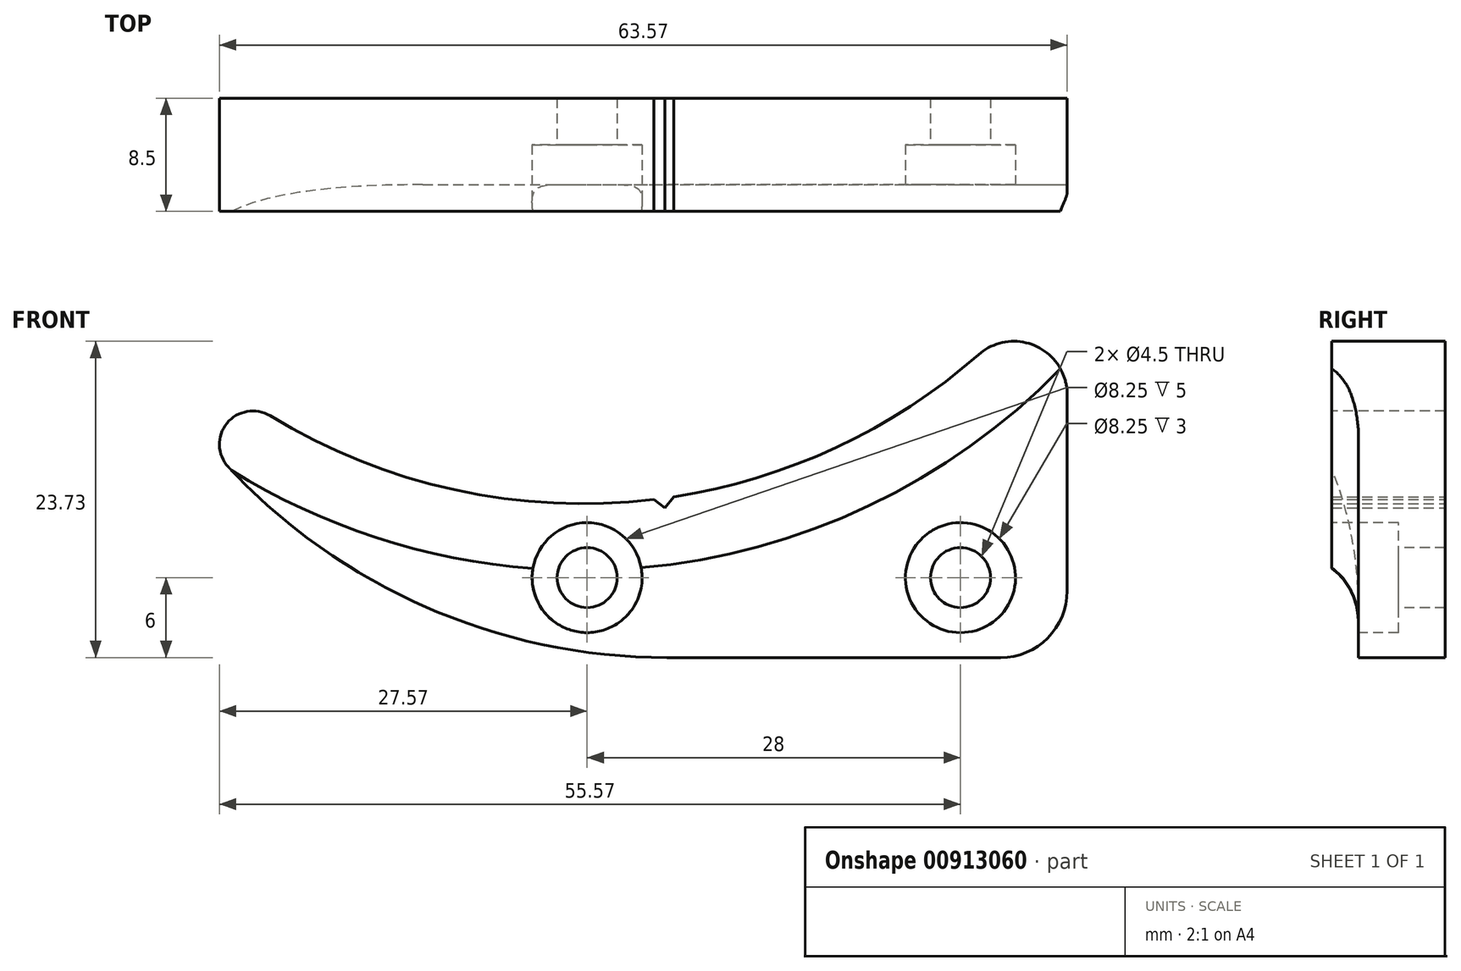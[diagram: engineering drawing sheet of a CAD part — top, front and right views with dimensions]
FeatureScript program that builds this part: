
annotation { "Feature Type Name" : "Feature", "Feature Type Description" : "" }
export const myFeature = defineFeature(function(context is Context, id is Id, definition is map)
    precondition{}
    {
        {
            var Q0;
            Q0=qCreatedBy(makeId("Front.planeOp"),FACE);
            var sketch = newSketch(context, id + "F0", { "sketchPlane" : qUnion([Q0])});
            skLineSegment(sketch, "E0", {"start": v(0, 30) * mm, "end": v(0, 0) * mm});
            skLineSegment(sketch, "E1", {"start": v(0, 0) * mm, "end": v(-30, 0) * mm});
            skArc(sketch, "E2", {"start": v(-72.2, 29.38) * mm, "mid": v(-55.71, 8.07) * mm, "end": v(-30, 0) * mm});
            skArc(sketch, "E3", {"start": v(-72.2, 29.38) * mm, "mid": v(-35.95, 11.55) * mm, "end": v(0, 30) * mm});
            skLineSegment(sketch, "E4", {"start": v(-30, 0) * mm, "end": v(-30, 12) * mm, "construction": true});
            skSolve(sketch);
        }
        {
            var Q0;
            Q0=makeQuery(id+"F0.imprint","IMPRINT",FACE,{"disambiguationData":[TD([[makeQuery(id+"F0.imprint","IMPRINT",EDGE,{"derivedFrom":sQuery(id+"F0.wireOp",EDGE,"E0")}),-1.0]])]});
            extrude(context, id + "F1", {"entities" : qUnion([Q0]), "depth" : 8.5 * mm, "offsetDistance" : 25 * mm});
        }
        {
            var Q0;
            Q0=makeQuery(id+"F1.opExtrude","SWEPT_EDGE",EDGE,{"disambiguationData":[OSD([sQuery(id+"F0.wireOp",EDGE,"E2"),sQuery(id+"F0.wireOp",EDGE,"E3")])]});
            fillet(context, id + "F2", {"entities" : qUnion([Q0]), "radius" : 2.5 * mm, "tangentPropagation" : true, "allowEdgeOverflow" : false});
        }
        {
            var Q0;
            Q0=makeQuery(id+"F1.opExtrude","SWEPT_EDGE",EDGE,{"disambiguationData":[OSD([sQuery(id+"F0.wireOp",EDGE,"E0"),sQuery(id+"F0.wireOp",EDGE,"E3")])]});
            fillet(context, id + "F3", {"entities" : qUnion([Q0]), "radius" : 4 * mm, "tangentPropagation" : true, "allowEdgeOverflow" : false});
        }
        {
            var Q0;
            Q0=makeQuery(id+"F1.opExtrude","CAP_FACE",FACE,{"disambiguationData":[OSD([sQuery(id+"F0.wireOp",EDGE,"E0"),sQuery(id+"F0.wireOp",EDGE,"E1"),sQuery(id+"F0.wireOp",EDGE,"E2"),sQuery(id+"F0.wireOp",EDGE,"E3")])],"isStart":false});
            var sketch = newSketch(context, id + "F4", { "sketchPlane" : qUnion([Q0])});
            skArc(sketch, "E5.0", {"start": v(-59.77, 18.14) * mm, "mid": v(-32.45, 11.72) * mm, "end": v(-6.64, 22.74) * mm, "construction": true});
            skArc(sketch, "E6.0", {"start": v(-62.67, 14.05) * mm, "mid": v(-30.24, 6.92) * mm, "end": v(-0.5, 21.68) * mm});
            skArc(sketch, "E7.0", {"start": v(-62.67, 14.05) * mm, "mid": v(-47.78, 3.66) * mm, "end": v(-30, 0) * mm});
            skLineSegment(sketch, "E8.0", {"start": v(0, 0) * mm, "end": v(-30, 0) * mm});
            skLineSegment(sketch, "E9.0", {"start": v(0, 19.73) * mm, "end": v(0, 0) * mm});
            skArc(sketch, "E10.0", {"start": v(0, 19.73) * mm, "mid": v(-0.13, 20.74) * mm, "end": v(-0.5, 21.68) * mm});
            skPoint(sketch, "E11.orphan", {"position": v(-62.9, 14.3) * mm});
            skSolve(sketch);
        }
        {
            var Q0;
            Q0=makeQuery(id+"F4.imprint","IMPRINT",FACE,{"disambiguationData":[TD([[makeQuery(id+"F4.imprint","IMPRINT",EDGE,{"derivedFrom":sQuery(id+"F4.wireOp",EDGE,"E6.0")}),-1.0]])]});
            extrude(context, id + "F5", {"entities" : qUnion([Q0]), "operationType" : NewBodyOperationType.REMOVE, "oppositeDirection" : true, "depth" : 2 * mm, "offsetDistance" : 25 * mm});
        }
        {
            var Q0;
            Q0=makeQuery(id+"F1.opExtrude","CAP_FACE",FACE,{"disambiguationData":[OSD([sQuery(id+"F0.wireOp",EDGE,"E0"),sQuery(id+"F0.wireOp",EDGE,"E1"),sQuery(id+"F0.wireOp",EDGE,"E2"),sQuery(id+"F0.wireOp",EDGE,"E3")])],"isStart":false});
            var sketch = newSketch(context, id + "F6", { "sketchPlane" : qUnion([Q0])});
            skPoint(sketch, "E12", {"position": v(-36, 6) * mm});
            skPoint(sketch, "E13", {"position": v(-8, 6) * mm});
            skSolve(sketch);
        }
        {
            var Q0;
            {var subQ0=sQuery(id+"F4.wireOp",EDGE,"E6.0");Q0=makeQuery(id+"F8.hole-1.boolean.opBoolean","SPLIT",EDGE,{"disambiguationData":[TD([makeQuery(id+"F1.opExtrude","SWEPT_FACE",FACE,{"disambiguationData":[OSD([sQuery(id+"F0.wireOp",EDGE,"E2")])]})])],"derivedFrom":makeQuery(id+"F5.boolean.opBoolean","COPY",EDGE,{"derivedFrom":makeQuery(id+"F5.opExtrude","CAP_EDGE",EDGE,{"disambiguationData":[OSD([subQ0])],"isStart":false})})});}
            fillet(context, id + "F7", {"entities" : qUnion([Q0]), "radius" : 5 * mm, "tangentPropagation" : true, "allowEdgeOverflow" : false});
        }
        {
            var Q0;
            Q0=sQuery(id+"F6.wireOp",VERTEX,"E13");
            var Q1;
            Q1=sQuery(id+"F6.wireOp",VERTEX,"E12");
            var Q2;
            Q2=makeQuery(id+"F1.opExtrude","SWEPT_BODY",BODY,{"disambiguationData":[OSD([sQuery(id+"F0.wireOp",EDGE,"E0"),sQuery(id+"F0.wireOp",EDGE,"E1"),sQuery(id+"F0.wireOp",EDGE,"E2"),sQuery(id+"F0.wireOp",EDGE,"E3")])]});
            hole(context, id + "F8", {"style" : HoleStyle.C_BORE, "endStyle" : HoleEndStyle.THROUGH, "holeDiameter" : 4.5 * mm, "cBoreDiameter" : 8.25 * mm, "cBoreDepth" : 5 * mm, "majorDiameter" : 5 * mm, "isTappedThrough" : true, "tappedDepth" : 16.25 * mm, "tapClearance" : 3, "startFromSketch" : true, "locations" : qUnion([Q0, Q1]), "scope" : qUnion([Q2])});
        }
        {
            var Q0;
            Q0=qCreatedBy(makeId("Front.planeOp"),FACE);
            var sketch = newSketch(context, id + "F9", { "sketchPlane" : qUnion([Q0])});
            skArc(sketch, "E14.0", {"start": v(-59.77, 18.14) * mm, "mid": v(-32.45, 11.72) * mm, "end": v(-6.64, 22.74) * mm, "construction": true});
            skLineSegment(sketch, "E15", {"start": v(-31, 11.87) * mm, "end": v(-30.16, 11.23) * mm});
            skLineSegment(sketch, "E16", {"start": v(-30.16, 11.23) * mm, "end": v(-29.51, 12.07) * mm});
            skLineSegment(sketch, "E17", {"start": v(-29.51, 12.07) * mm, "end": v(-31, 11.87) * mm});
            skLineSegment(sketch, "E18", {"start": v(-31, 11.87) * mm, "end": v(-29.51, 12.07) * mm});
            skLineSegment(sketch, "E19", {"start": v(-30.16, 11.23) * mm, "end": v(-36.33, 56.55) * mm, "construction": true});
            skSolve(sketch);
        }
        {
            var Q0;
            Q0=makeQuery(id+"F9.imprint","IMPRINT",FACE,{"disambiguationData":[TD([[makeQuery(id+"F9.imprint","IMPRINT",EDGE,{"derivedFrom":sQuery(id+"F9.wireOp",EDGE,"E15")}),1.0]])]});
            extrude(context, id + "F10", {"entities" : qUnion([Q0]), "operationType" : NewBodyOperationType.REMOVE, "endBound" : BoundingType.THROUGH_ALL, "depth" : 25 * mm, "offsetDistance" : 25 * mm});
        }
        {
            var Q0;
            Q0=makeQuery(id+"F1.opExtrude","SWEPT_EDGE",EDGE,{"disambiguationData":[OSD([sQuery(id+"F0.wireOp",EDGE,"E0"),sQuery(id+"F0.wireOp",EDGE,"E1")])]});
            fillet(context, id + "F11", {"entities" : qUnion([Q0]), "radius" : 5 * mm, "tangentPropagation" : true, "allowEdgeOverflow" : false});
        }
    });
